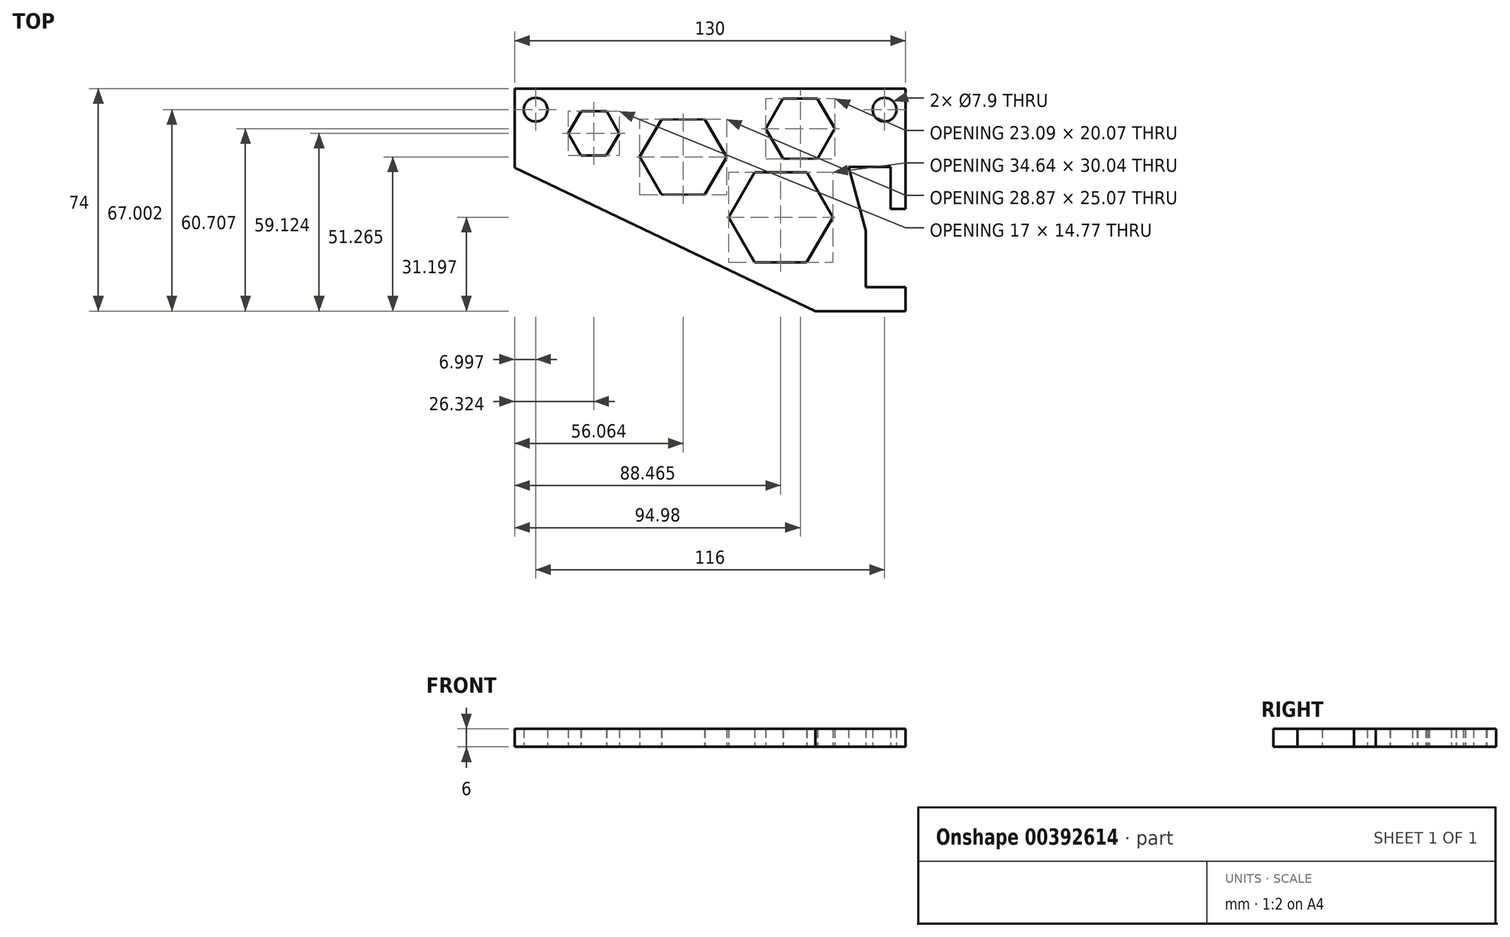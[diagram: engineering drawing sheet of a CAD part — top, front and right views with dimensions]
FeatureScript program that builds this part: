
annotation { "Feature Type Name" : "Feature", "Feature Type Description" : "" }
export const myFeature = defineFeature(function(context is Context, id is Id, definition is map)
    precondition{}
    {
        {
            var Q0;
            Q0=qCreatedBy(makeId("Top.planeOp"),FACE);
            var sketch = newSketch(context, id + "F0", { "sketchPlane" : qUnion([Q0])});
            skLineSegment(sketch, "E0.bottom", {"start": v(-76.15, 30.72) * mm, "end": v(53.85, 30.72) * mm});
            skLineSegment(sketch, "E1", {"start": v(53.85, 30.72) * mm, "end": v(53.85, -9.28) * mm});
            skLineSegment(sketch, "E2", {"start": v(53.85, -9.28) * mm, "end": v(48.85, -9.28) * mm});
            skLineSegment(sketch, "E3", {"start": v(48.85, -9.28) * mm, "end": v(48.85, 4.72) * mm});
            skLineSegment(sketch, "E4", {"start": v(48.85, 4.72) * mm, "end": v(34.85, 4.72) * mm});
            skLineSegment(sketch, "E5", {"start": v(40.65, -35.28) * mm, "end": v(53.85, -35.28) * mm});
            skLineSegment(sketch, "E6", {"start": v(53.85, -35.28) * mm, "end": v(53.85, -43.28) * mm});
            skLineSegment(sketch, "E7", {"start": v(40.65, -35.28) * mm, "end": v(40.65, -16.5) * mm});
            skLineSegment(sketch, "E8", {"start": v(40.65, -16.5) * mm, "end": v(34.85, 4.72) * mm});
            skLineSegment(sketch, "E9", {"start": v(53.85, -43.28) * mm, "end": v(23.85, -43.28) * mm});
            skLineSegment(sketch, "E10", {"start": v(23.85, -43.28) * mm, "end": v(-76.15, 4.44) * mm});
            skLineSegment(sketch, "E11", {"start": v(-76.15, 30.72) * mm, "end": v(-76.15, 4.44) * mm});
            skCircle(sketch, "E12", {"center": v(-69.15, 23.72) * mm, "radius": 3.95 * mm});
            skCircle(sketch, "E13", {"center": v(46.85, 23.72) * mm, "radius": 3.95 * mm});
            skCircle(sketch, "E14.cCircle", {"center": v(-49.83, 15.84) * mm, "radius": 8.5 * mm, "construction": true});
            skLineSegment(sketch, "E14.0", {"start": v(-45.62, 8.46) * mm, "end": v(-54.12, 8.5) * mm});
            skLineSegment(sketch, "E14.1", {"start": v(-54.12, 8.5) * mm, "end": v(-58.33, 15.9) * mm});
            skLineSegment(sketch, "E14.2", {"start": v(-58.33, 15.9) * mm, "end": v(-54.03, 23.23) * mm});
            skLineSegment(sketch, "E14.3", {"start": v(-54.03, 23.23) * mm, "end": v(-45.53, 23.18) * mm});
            skLineSegment(sketch, "E14.4", {"start": v(-45.53, 23.18) * mm, "end": v(-41.33, 15.8) * mm});
            skLineSegment(sketch, "E14.5", {"start": v(-41.33, 15.8) * mm, "end": v(-45.62, 8.46) * mm});
            skCircle(sketch, "E15.cCircle", {"center": v(-20.09, 7.99) * mm, "radius": 14.43 * mm, "construction": true});
            skLineSegment(sketch, "E15.0", {"start": v(-12.93, -4.55) * mm, "end": v(-27.36, -4.48) * mm});
            skLineSegment(sketch, "E15.1", {"start": v(-27.36, -4.48) * mm, "end": v(-34.52, 8.05) * mm});
            skLineSegment(sketch, "E15.2", {"start": v(-34.52, 8.05) * mm, "end": v(-27.25, 20.52) * mm});
            skLineSegment(sketch, "E15.3", {"start": v(-27.25, 20.52) * mm, "end": v(-12.81, 20.45) * mm});
            skLineSegment(sketch, "E15.4", {"start": v(-12.81, 20.45) * mm, "end": v(-5.65, 7.92) * mm});
            skLineSegment(sketch, "E15.5", {"start": v(-5.65, 7.92) * mm, "end": v(-12.93, -4.55) * mm});
            skCircle(sketch, "E16.cCircle", {"center": v(12.31, -12.08) * mm, "radius": 17.32 * mm, "construction": true});
            skLineSegment(sketch, "E16.0", {"start": v(20.94, -27.1) * mm, "end": v(3.62, -27.06) * mm});
            skLineSegment(sketch, "E16.1", {"start": v(3.62, -27.06) * mm, "end": v(-5, -12.05) * mm});
            skLineSegment(sketch, "E16.2", {"start": v(-5, -12.05) * mm, "end": v(3.69, 2.94) * mm});
            skLineSegment(sketch, "E16.3", {"start": v(3.69, 2.94) * mm, "end": v(21, 2.9) * mm});
            skLineSegment(sketch, "E16.4", {"start": v(21, 2.9) * mm, "end": v(29.63, -12.12) * mm});
            skLineSegment(sketch, "E16.5", {"start": v(29.63, -12.12) * mm, "end": v(20.94, -27.1) * mm});
            skCircle(sketch, "E17.cCircle", {"center": v(18.83, 17.43) * mm, "radius": 10 * mm, "construction": true});
            skLineSegment(sketch, "E17.0", {"start": v(13, 27.4) * mm, "end": v(7.28, 17.35) * mm});
            skLineSegment(sketch, "E17.1", {"start": v(24.54, 27.46) * mm, "end": v(13, 27.4) * mm});
            skLineSegment(sketch, "E17.2", {"start": v(30.38, 17.5) * mm, "end": v(24.54, 27.46) * mm});
            skLineSegment(sketch, "E17.3", {"start": v(24.67, 7.46) * mm, "end": v(30.38, 17.5) * mm});
            skLineSegment(sketch, "E17.4", {"start": v(13.12, 7.4) * mm, "end": v(24.67, 7.46) * mm});
            skLineSegment(sketch, "E17.5", {"start": v(7.28, 17.35) * mm, "end": v(13.12, 7.4) * mm});
            skPoint(sketch, "E17.0.midPoint", {"position": v(10.14, 22.37) * mm});
            skSolve(sketch);
        }
        {
            var Q0;
            Q0=makeQuery(id+"F0.imprint","IMPRINT",FACE,{"disambiguationData":[TD([[makeQuery(id+"F0.imprint","IMPRINT",EDGE,{"derivedFrom":sQuery(id+"F0.wireOp",EDGE,"E0.bottom")}),-1.0]])]});
            extrude(context, id + "F1", {"entities" : qUnion([Q0]), "depth" : 6 * mm});
        }
    });
